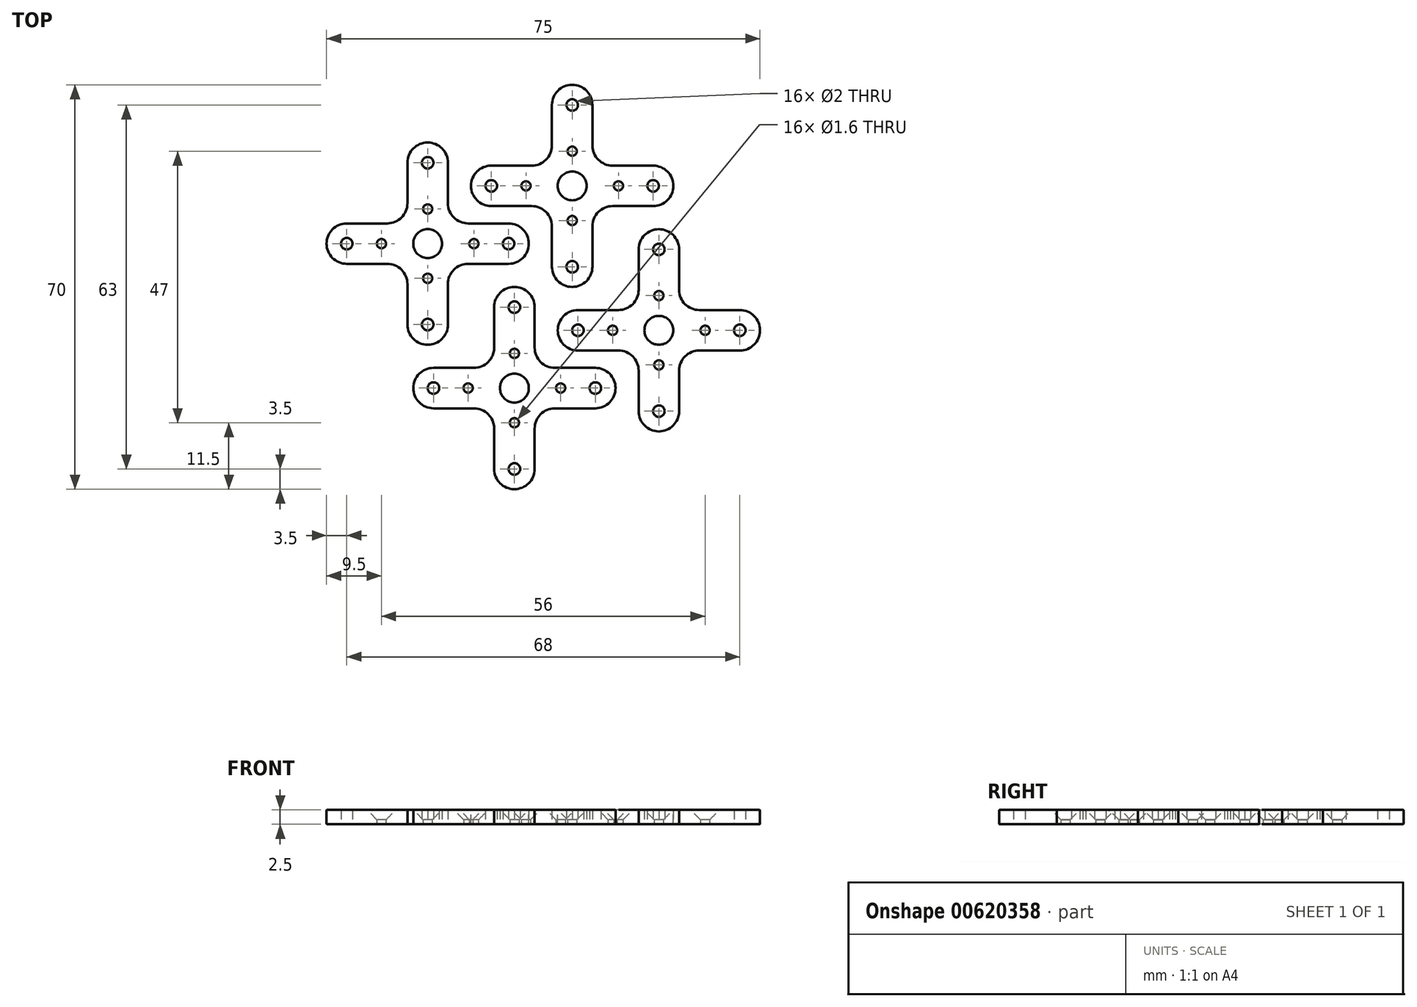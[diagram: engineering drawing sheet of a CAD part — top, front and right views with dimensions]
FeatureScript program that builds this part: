
annotation { "Feature Type Name" : "Feature", "Feature Type Description" : "" }
export const myFeature = defineFeature(function(context is Context, id is Id, definition is map)
    precondition{}
    {
        {
            var Q0;
            Q0=qCreatedBy(makeId("Top.planeOp"),FACE);
            var sketch = newSketch(context, id + "F0", { "sketchPlane" : qUnion([Q0])});
            skLineSegment(sketch, "E0.bottom", {"start": v(-17.84, -37.87) * mm, "end": v(-24.84, -37.87) * mm});
            skLineSegment(sketch, "E0.top", {"start": v(-17.84, -2.87) * mm, "end": v(-24.84, -2.87) * mm});
            skLineSegment(sketch, "E0.left", {"start": v(-3.84, -23.87) * mm, "end": v(-3.84, -16.87) * mm});
            skLineSegment(sketch, "E0.right", {"start": v(-38.84, -23.87) * mm, "end": v(-38.84, -16.87) * mm});
            skPoint(sketch, "E0.middle", {"position": v(-21.34, -20.37) * mm});
            skCircle(sketch, "E1", {"center": v(-21.34, -20.37) * mm, "radius": 2.5 * mm});
            skLineSegment(sketch, "E2", {"start": v(-38.84, -23.87) * mm, "end": v(-24.84, -23.87) * mm});
            skLineSegment(sketch, "E3", {"start": v(-24.84, -23.87) * mm, "end": v(-24.84, -37.87) * mm});
            skPoint(sketch, "E4.orphan", {"position": v(-38.84, -37.87) * mm});
            skLineSegment(sketch, "E5", {"start": v(-24.84, -2.87) * mm, "end": v(-24.84, -16.87) * mm});
            skLineSegment(sketch, "E6", {"start": v(-24.84, -16.87) * mm, "end": v(-38.84, -16.87) * mm});
            skLineSegment(sketch, "E7", {"start": v(-17.84, -2.87) * mm, "end": v(-17.84, -16.87) * mm});
            skLineSegment(sketch, "E8", {"start": v(-17.84, -16.87) * mm, "end": v(-3.84, -16.87) * mm});
            skLineSegment(sketch, "E9", {"start": v(-3.84, -23.87) * mm, "end": v(-17.84, -23.87) * mm});
            skLineSegment(sketch, "E10", {"start": v(-17.84, -23.87) * mm, "end": v(-17.84, -37.87) * mm});
            skPoint(sketch, "E11.orphan", {"position": v(-38.84, -2.87) * mm});
            skPoint(sketch, "E12.orphan", {"position": v(-3.84, -2.87) * mm});
            skPoint(sketch, "E13.orphan", {"position": v(-3.84, -37.87) * mm});
            skCircle(sketch, "E14", {"center": v(-7.34, -20.37) * mm, "radius": 1 * mm});
            skCircle(sketch, "E15", {"center": v(-35.34, -20.37) * mm, "radius": 1 * mm});
            skCircle(sketch, "E16", {"center": v(-21.34, -6.37) * mm, "radius": 1 * mm});
            skCircle(sketch, "E17", {"center": v(-21.34, -34.37) * mm, "radius": 1 * mm});
            skCircle(sketch, "E18", {"center": v(-13.34, -20.37) * mm, "radius": 0.8 * mm});
            skCircle(sketch, "E19", {"center": v(-29.34, -20.37) * mm, "radius": 0.8 * mm});
            skCircle(sketch, "E20", {"center": v(-21.34, -14.37) * mm, "radius": 0.8 * mm});
            skCircle(sketch, "E21", {"center": v(-21.34, -26.37) * mm, "radius": 0.8 * mm});
            skSolve(sketch);
        }
        {
            var Q0;
            Q0=makeQuery(id+"F0.imprint","IMPRINT",FACE,{"disambiguationData":[TD([[makeQuery(id+"F0.imprint","IMPRINT",EDGE,{"derivedFrom":sQuery(id+"F0.wireOp",EDGE,"E0.bottom")}),-1.0]])]});
            extrude(context, id + "F1", {"entities" : qUnion([Q0]), "depth" : 2.5 * mm});
        }
        {
            var Q0;
            Q0=makeQuery(id+"F1.opExtrude","SWEPT_EDGE",EDGE,{"disambiguationData":[OSD([sQuery(id+"F0.wireOp",EDGE,"E0.top"),sQuery(id+"F0.wireOp",EDGE,"E5")])]});
            var Q1;
            Q1=makeQuery(id+"F1.opExtrude","SWEPT_EDGE",EDGE,{"disambiguationData":[OSD([sQuery(id+"F0.wireOp",EDGE,"E0.top"),sQuery(id+"F0.wireOp",EDGE,"E7")])]});
            var Q2;
            Q2=makeQuery(id+"F1.opExtrude","SWEPT_EDGE",EDGE,{"disambiguationData":[OSD([sQuery(id+"F0.wireOp",EDGE,"E0.left"),sQuery(id+"F0.wireOp",EDGE,"E8")])]});
            var Q3;
            Q3=makeQuery(id+"F1.opExtrude","SWEPT_EDGE",EDGE,{"disambiguationData":[OSD([sQuery(id+"F0.wireOp",EDGE,"E0.left"),sQuery(id+"F0.wireOp",EDGE,"E9")])]});
            var Q4;
            Q4=makeQuery(id+"F1.opExtrude","SWEPT_EDGE",EDGE,{"disambiguationData":[OSD([sQuery(id+"F0.wireOp",EDGE,"E0.bottom"),sQuery(id+"F0.wireOp",EDGE,"E10")])]});
            var Q5;
            Q5=makeQuery(id+"F1.opExtrude","SWEPT_EDGE",EDGE,{"disambiguationData":[OSD([sQuery(id+"F0.wireOp",EDGE,"E0.bottom"),sQuery(id+"F0.wireOp",EDGE,"E3")])]});
            var Q6;
            Q6=makeQuery(id+"F1.opExtrude","SWEPT_EDGE",EDGE,{"disambiguationData":[OSD([sQuery(id+"F0.wireOp",EDGE,"E0.right"),sQuery(id+"F0.wireOp",EDGE,"E2")])]});
            var Q7;
            Q7=makeQuery(id+"F1.opExtrude","SWEPT_EDGE",EDGE,{"disambiguationData":[OSD([sQuery(id+"F0.wireOp",EDGE,"E0.right"),sQuery(id+"F0.wireOp",EDGE,"E6")])]});
            var Q8;
            Q8=makeQuery(id+"F1.opExtrude","SWEPT_EDGE",EDGE,{"disambiguationData":[OSD([sQuery(id+"F0.wireOp",EDGE,"E2"),sQuery(id+"F0.wireOp",EDGE,"E3")])]});
            var Q9;
            Q9=makeQuery(id+"F1.opExtrude","SWEPT_EDGE",EDGE,{"disambiguationData":[OSD([sQuery(id+"F0.wireOp",EDGE,"E9"),sQuery(id+"F0.wireOp",EDGE,"E10")])]});
            var Q10;
            Q10=makeQuery(id+"F1.opExtrude","SWEPT_EDGE",EDGE,{"disambiguationData":[OSD([sQuery(id+"F0.wireOp",EDGE,"E7"),sQuery(id+"F0.wireOp",EDGE,"E8")])]});
            var Q11;
            Q11=makeQuery(id+"F1.opExtrude","SWEPT_EDGE",EDGE,{"disambiguationData":[OSD([sQuery(id+"F0.wireOp",EDGE,"E5"),sQuery(id+"F0.wireOp",EDGE,"E6")])]});
            fillet(context, id + "F2", {"entities" : qUnion([Q0, Q1, Q2, Q3, Q4, Q5, Q6, Q7, Q8, Q9, Q10, Q11]), "radius" : 3.5 * mm, "tangentPropagation" : true, "allowEdgeOverflow" : false});
        }
        {
            var Q0;
            Q0=makeQuery(id+"F1.opExtrude","CAP_EDGE",EDGE,{"disambiguationData":[OSD([sQuery(id+"F0.wireOp",EDGE,"E20")])],"isStart":false});
            var Q1;
            Q1=makeQuery(id+"F1.opExtrude","CAP_EDGE",EDGE,{"disambiguationData":[OSD([sQuery(id+"F0.wireOp",EDGE,"E18")])],"isStart":false});
            var Q2;
            Q2=makeQuery(id+"F1.opExtrude","CAP_EDGE",EDGE,{"disambiguationData":[OSD([sQuery(id+"F0.wireOp",EDGE,"E21")])],"isStart":false});
            var Q3;
            Q3=makeQuery(id+"F1.opExtrude","CAP_EDGE",EDGE,{"disambiguationData":[OSD([sQuery(id+"F0.wireOp",EDGE,"E19")])],"isStart":false});
            chamfer(context, id + "F3", {"entities" : qUnion([Q0, Q1, Q2, Q3]), "width" : 1.7 * mm, "tangentPropagation" : true});
        }
        {
            var Q0;
            Q0=makeQuery(id+"F1.opExtrude","CAP_FACE",FACE,{"disambiguationData":[OSD([sQuery(id+"F0.wireOp",EDGE,"E0.bottom"),sQuery(id+"F0.wireOp",EDGE,"E0.top"),sQuery(id+"F0.wireOp",EDGE,"E0.left"),sQuery(id+"F0.wireOp",EDGE,"E0.right"),sQuery(id+"F0.wireOp",EDGE,"E1"),sQuery(id+"F0.wireOp",EDGE,"E2"),sQuery(id+"F0.wireOp",EDGE,"E3"),sQuery(id+"F0.wireOp",EDGE,"E5"),sQuery(id+"F0.wireOp",EDGE,"E6"),sQuery(id+"F0.wireOp",EDGE,"E7"),sQuery(id+"F0.wireOp",EDGE,"E8"),sQuery(id+"F0.wireOp",EDGE,"E9"),sQuery(id+"F0.wireOp",EDGE,"E10"),sQuery(id+"F0.wireOp",EDGE,"E14"),sQuery(id+"F0.wireOp",EDGE,"E15"),sQuery(id+"F0.wireOp",EDGE,"E16"),sQuery(id+"F0.wireOp",EDGE,"E17"),sQuery(id+"F0.wireOp",EDGE,"E18"),sQuery(id+"F0.wireOp",EDGE,"E19"),sQuery(id+"F0.wireOp",EDGE,"E20"),sQuery(id+"F0.wireOp",EDGE,"E21")])],"isStart":false});
            var Q1;
            Q1=makeQuery(id+"F1.opExtrude","CAP_FACE",FACE,{"disambiguationData":[OSD([sQuery(id+"F0.wireOp",EDGE,"E0.bottom"),sQuery(id+"F0.wireOp",EDGE,"E0.top"),sQuery(id+"F0.wireOp",EDGE,"E0.left"),sQuery(id+"F0.wireOp",EDGE,"E0.right"),sQuery(id+"F0.wireOp",EDGE,"E1"),sQuery(id+"F0.wireOp",EDGE,"E2"),sQuery(id+"F0.wireOp",EDGE,"E3"),sQuery(id+"F0.wireOp",EDGE,"E5"),sQuery(id+"F0.wireOp",EDGE,"E6"),sQuery(id+"F0.wireOp",EDGE,"E7"),sQuery(id+"F0.wireOp",EDGE,"E8"),sQuery(id+"F0.wireOp",EDGE,"E9"),sQuery(id+"F0.wireOp",EDGE,"E10"),sQuery(id+"F0.wireOp",EDGE,"E14"),sQuery(id+"F0.wireOp",EDGE,"E15"),sQuery(id+"F0.wireOp",EDGE,"E16"),sQuery(id+"F0.wireOp",EDGE,"E17"),sQuery(id+"F0.wireOp",EDGE,"E18"),sQuery(id+"F0.wireOp",EDGE,"E19"),sQuery(id+"F0.wireOp",EDGE,"E20"),sQuery(id+"F0.wireOp",EDGE,"E21")])],"isStart":true});
            fillet(context, id + "F4", {"entities" : qUnion([Q0, Q1]), "radius" : 0.15 * mm, "tangentPropagation" : true, "allowEdgeOverflow" : false});
        }
        {
            var Q0;
            Q0=makeQuery(id+"F1.opExtrude","SWEPT_BODY",BODY,{"disambiguationData":[OSD([sQuery(id+"F0.wireOp",EDGE,"E0.bottom"),sQuery(id+"F0.wireOp",EDGE,"E0.top"),sQuery(id+"F0.wireOp",EDGE,"E0.left"),sQuery(id+"F0.wireOp",EDGE,"E0.right"),sQuery(id+"F0.wireOp",EDGE,"E1"),sQuery(id+"F0.wireOp",EDGE,"E2"),sQuery(id+"F0.wireOp",EDGE,"E3"),sQuery(id+"F0.wireOp",EDGE,"E5"),sQuery(id+"F0.wireOp",EDGE,"E6"),sQuery(id+"F0.wireOp",EDGE,"E7"),sQuery(id+"F0.wireOp",EDGE,"E8"),sQuery(id+"F0.wireOp",EDGE,"E9"),sQuery(id+"F0.wireOp",EDGE,"E10"),sQuery(id+"F0.wireOp",EDGE,"E14"),sQuery(id+"F0.wireOp",EDGE,"E15"),sQuery(id+"F0.wireOp",EDGE,"E16"),sQuery(id+"F0.wireOp",EDGE,"E17"),sQuery(id+"F0.wireOp",EDGE,"E18"),sQuery(id+"F0.wireOp",EDGE,"E19"),sQuery(id+"F0.wireOp",EDGE,"E20"),sQuery(id+"F0.wireOp",EDGE,"E21")])]});
            transform(context, id + "F5", {"entities" : qUnion([Q0]), "transformType" : TransformType.TRANSLATION_3D, "dx" : 25 * mm, "dy" : 10 * mm, "dz" : 0 * mm, "makeCopy" : true});
        }
        {
            var Q0;
            Q0=makeQuery(id+"F1.opExtrude","SWEPT_BODY",BODY,{"disambiguationData":[OSD([sQuery(id+"F0.wireOp",EDGE,"E0.bottom"),sQuery(id+"F0.wireOp",EDGE,"E0.top"),sQuery(id+"F0.wireOp",EDGE,"E0.left"),sQuery(id+"F0.wireOp",EDGE,"E0.right"),sQuery(id+"F0.wireOp",EDGE,"E1"),sQuery(id+"F0.wireOp",EDGE,"E2"),sQuery(id+"F0.wireOp",EDGE,"E3"),sQuery(id+"F0.wireOp",EDGE,"E5"),sQuery(id+"F0.wireOp",EDGE,"E6"),sQuery(id+"F0.wireOp",EDGE,"E7"),sQuery(id+"F0.wireOp",EDGE,"E8"),sQuery(id+"F0.wireOp",EDGE,"E9"),sQuery(id+"F0.wireOp",EDGE,"E10"),sQuery(id+"F0.wireOp",EDGE,"E14"),sQuery(id+"F0.wireOp",EDGE,"E15"),sQuery(id+"F0.wireOp",EDGE,"E16"),sQuery(id+"F0.wireOp",EDGE,"E17"),sQuery(id+"F0.wireOp",EDGE,"E18"),sQuery(id+"F0.wireOp",EDGE,"E19"),sQuery(id+"F0.wireOp",EDGE,"E20"),sQuery(id+"F0.wireOp",EDGE,"E21")])]});
            transform(context, id + "F6", {"entities" : qUnion([Q0]), "transformType" : TransformType.TRANSLATION_3D, "dx" : 15 * mm, "dy" : -25 * mm, "dz" : 0 * mm, "makeCopy" : true});
        }
        {
            var Q0;
            Q0=makeQuery(id+"F6.opPattern","COPY",BODY,{"derivedFrom":makeQuery(id+"F1.opExtrude","SWEPT_BODY",BODY,{"disambiguationData":[OSD([sQuery(id+"F0.wireOp",EDGE,"E0.bottom"),sQuery(id+"F0.wireOp",EDGE,"E0.top"),sQuery(id+"F0.wireOp",EDGE,"E0.left"),sQuery(id+"F0.wireOp",EDGE,"E0.right"),sQuery(id+"F0.wireOp",EDGE,"E1"),sQuery(id+"F0.wireOp",EDGE,"E2"),sQuery(id+"F0.wireOp",EDGE,"E3"),sQuery(id+"F0.wireOp",EDGE,"E5"),sQuery(id+"F0.wireOp",EDGE,"E6"),sQuery(id+"F0.wireOp",EDGE,"E7"),sQuery(id+"F0.wireOp",EDGE,"E8"),sQuery(id+"F0.wireOp",EDGE,"E9"),sQuery(id+"F0.wireOp",EDGE,"E10"),sQuery(id+"F0.wireOp",EDGE,"E14"),sQuery(id+"F0.wireOp",EDGE,"E15"),sQuery(id+"F0.wireOp",EDGE,"E16"),sQuery(id+"F0.wireOp",EDGE,"E17"),sQuery(id+"F0.wireOp",EDGE,"E18"),sQuery(id+"F0.wireOp",EDGE,"E19"),sQuery(id+"F0.wireOp",EDGE,"E20"),sQuery(id+"F0.wireOp",EDGE,"E21")])]}),"instanceName":"1"});
            transform(context, id + "F7", {"entities" : qUnion([Q0]), "transformType" : TransformType.TRANSLATION_3D, "dx" : 25 * mm, "dy" : 10 * mm, "dz" : 0 * mm, "makeCopy" : true});
        }
    });
